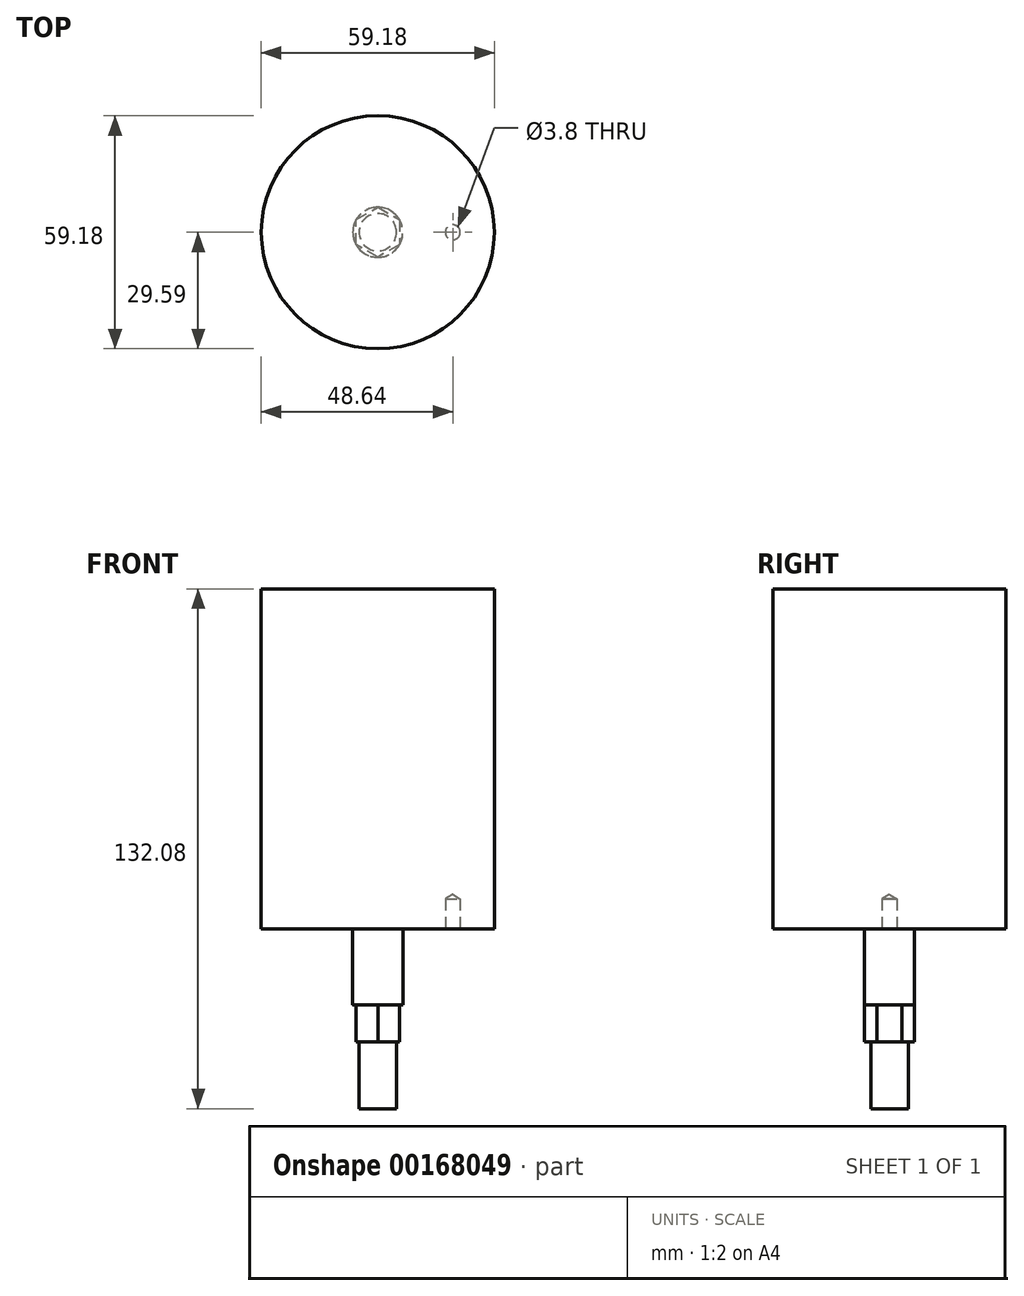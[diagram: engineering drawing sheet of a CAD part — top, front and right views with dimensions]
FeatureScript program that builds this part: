
annotation { "Feature Type Name" : "Feature", "Feature Type Description" : "" }
export const myFeature = defineFeature(function(context is Context, id is Id, definition is map)
    precondition{}
    {
        {
            var Q0;
            Q0=qCreatedBy(makeId("Top.planeOp"),FACE);
            var sketch = newSketch(context, id + "F0", { "sketchPlane" : qUnion([Q0])});
            skCircle(sketch, "E0", {"center": v(0, 0) * mm, "radius": 29.6 * mm});
            skSolve(sketch);
        }
        {
            var Q0;
            Q0 = qSketchRegion(id + "F0", true);
            extrude(context, id + "F1", {"entities" : qUnion([Q0]), "depth" : 86.36 * mm});
        }
        {
            var Q0;
            Q0=makeQuery(id+"F1.opExtrude","CAP_FACE",FACE,{"disambiguationData":[OSD([sQuery(id+"F0.wireOp",EDGE,"E0")])],"isStart":true});
            var sketch = newSketch(context, id + "F2", { "sketchPlane" : qUnion([Q0])});
            skCircle(sketch, "E1", {"center": v(0, 0) * mm, "radius": 6.35 * mm});
            skSolve(sketch);
        }
        {
            var Q0;
            Q0 = qSketchRegion(id + "F2", true);
            extrude(context, id + "F3", {"entities" : qUnion([Q0]), "operationType" : NewBodyOperationType.ADD, "depth" : 45.72 * mm});
        }
        {
            var Q0;
            Q0=makeQuery(id+"F1.opExtrude","CAP_FACE",FACE,{"disambiguationData":[OSD([sQuery(id+"F0.wireOp",EDGE,"E0")])],"isStart":true});
            var sketch = newSketch(context, id + "F4", { "sketchPlane" : qUnion([Q0])});
            skPoint(sketch, "E2", {"position": v(19.05, 0) * mm});
            skSolve(sketch);
        }
        {
            var Q0;
            Q0=sQuery(id+"F4.wireOp",VERTEX,"E2");
            var Q1;
            Q1=makeQuery(id+"F1.opExtrude","SWEPT_BODY",BODY,{"disambiguationData":[OSD([sQuery(id+"F0.wireOp",EDGE,"E0")])]});
            hole(context, id + "F5", {"style" : HoleStyle.SIMPLE, "endStyle" : HoleEndStyle.BLIND, "standardTappedOrClearance" : lookupTablePath({ "standard" : "ANSI", "engagement" : "75%", "pitch" : "24 tpi", "size" : "#10", "type" : "Tapped" }), "standardBlindInLast" : lookupTablePath({ "standard" : "ANSI", "engagement" : "75%", "pitch" : "24 tpi", "size" : "#10", "type" : "Tapped" }), "holeDiameter" : 3.8 * mm, "holeDepth" : 7.62 * mm, "locations" : qUnion([Q0]), "scope" : qUnion([Q1]), "majorDiameter" : 4.83 * mm});
        }
        {
            var Q0;
            Q0=qCreatedBy(makeId("Front.planeOp"),FACE);
            var sketch = newSketch(context, id + "F6", { "sketchPlane" : qUnion([Q0])});
            skLineSegment(sketch, "E3", {"start": v(0, 0) * mm, "end": v(0, -23.14) * mm, "construction": true});
            skSolve(sketch);
        }
        {
            var Q0;
            Q0=makeQuery(id+"F3.opExtrude","CAP_FACE",FACE,{"disambiguationData":[OSD([sQuery(id+"F2.wireOp",EDGE,"E1")])],"isStart":false});
            var sketch = newSketch(context, id + "F7", { "sketchPlane" : qUnion([Q0])});
            skCircle(sketch, "E4.cCircle", {"center": v(0, 0) * mm, "radius": 6.35 * mm, "construction": true});
            skLineSegment(sketch, "E4.0", {"start": v(5.5, -3.17) * mm, "end": v(0, -6.35) * mm});
            skLineSegment(sketch, "E4.1", {"start": v(0, -6.35) * mm, "end": v(-5.5, -3.18) * mm});
            skLineSegment(sketch, "E4.2", {"start": v(-5.5, -3.18) * mm, "end": v(-5.5, 3.18) * mm});
            skLineSegment(sketch, "E4.3", {"start": v(-5.5, 3.17) * mm, "end": v(0, 6.35) * mm});
            skLineSegment(sketch, "E4.4", {"start": v(0, 6.35) * mm, "end": v(5.5, 3.18) * mm});
            skLineSegment(sketch, "E4.5", {"start": v(5.5, 3.17) * mm, "end": v(5.5, -3.18) * mm});
            skCircle(sketch, "E5", {"center": v(0, 0) * mm, "radius": 14.18 * mm});
            skSolve(sketch);
        }
        {
            var Q0;
            Q0 = qSketchRegion(id + "F7", true);
            extrude(context, id + "F8", {"entities" : qUnion([Q0]), "operationType" : NewBodyOperationType.REMOVE, "oppositeDirection" : true, "depth" : 26.42 * mm});
        }
        {
            var Q0;
            Q0=makeQuery(id+"F3.opExtrude","CAP_FACE",FACE,{"disambiguationData":[OSD([sQuery(id+"F2.wireOp",EDGE,"E1")])],"isStart":false});
            var sketch = newSketch(context, id + "F9", { "sketchPlane" : qUnion([Q0])});
            skCircle(sketch, "E6", {"center": v(0, 0) * mm, "radius": 4.76 * mm});
            skCircle(sketch, "E7", {"center": v(0, 0) * mm, "radius": 11.91 * mm});
            skSolve(sketch);
        }
        {
            var Q0;
            Q0 = qSketchRegion(id + "F9", true);
            extrude(context, id + "F10", {"entities" : qUnion([Q0]), "operationType" : NewBodyOperationType.REMOVE, "oppositeDirection" : true, "depth" : 17.02 * mm});
        }
    });
